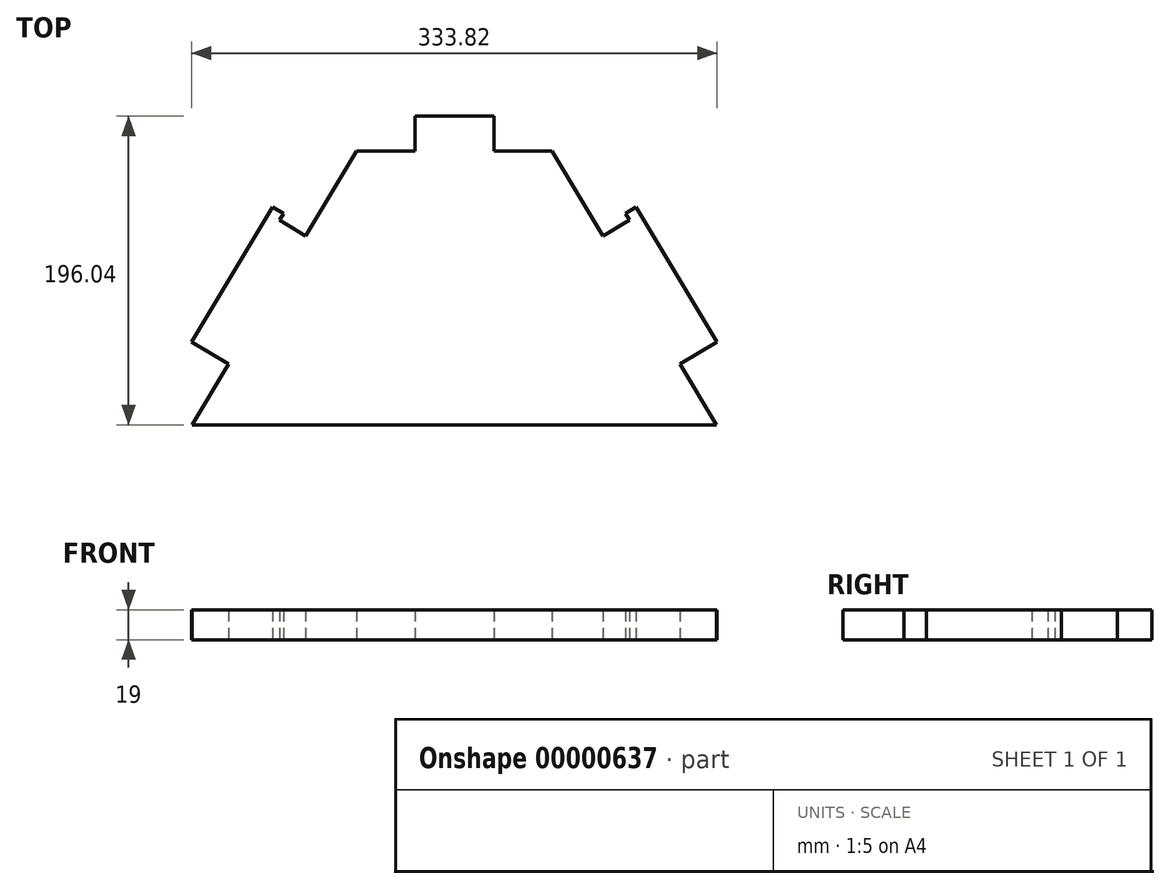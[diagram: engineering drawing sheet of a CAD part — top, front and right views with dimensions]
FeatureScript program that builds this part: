
annotation { "Feature Type Name" : "Feature", "Feature Type Description" : "" }
export const myFeature = defineFeature(function(context is Context, id is Id, definition is map)
    precondition{}
    {
        {
            var Q0;
            Q0=qCreatedBy(makeId("Top.planeOp"),FACE);
            var sketch = newSketch(context, id + "F0", { "sketchPlane" : qUnion([Q0])});
            skLineSegment(sketch, "E0", {"start": v(0, 22) * mm, "end": v(25, 22) * mm});
            skLineSegment(sketch, "E1", {"start": v(25, 22) * mm, "end": v(25, 0) * mm});
            skLineSegment(sketch, "E2", {"start": v(25, 0) * mm, "end": v(62, 0) * mm});
            skLineSegment(sketch, "E3", {"start": v(62, 0) * mm, "end": v(94.43, -54.01) * mm});
            skLineSegment(sketch, "E4", {"start": v(94.43, -54.01) * mm, "end": v(111.15, -43.97) * mm});
            skLineSegment(sketch, "E5", {"start": v(111.15, -43.97) * mm, "end": v(108.57, -39.69) * mm});
            skLineSegment(sketch, "E6", {"start": v(108.57, -39.69) * mm, "end": v(115.43, -35.57) * mm});
            skLineSegment(sketch, "E7", {"start": v(115.43, -35.57) * mm, "end": v(166.91, -121.3) * mm});
            skLineSegment(sketch, "E8", {"start": v(166.91, -121.3) * mm, "end": v(143.33, -135.46) * mm});
            skLineSegment(sketch, "E9", {"start": v(143.33, -135.46) * mm, "end": v(166.5, -174.04) * mm});
            skLineSegment(sketch, "E10", {"start": v(166.5, -174.04) * mm, "end": v(0, -174.04) * mm});
            skLineSegment(sketch, "E11", {"start": v(0, 22) * mm, "end": v(0, -174.04) * mm, "construction": true});
            skLineSegment(sketch, "E12.0.MirrorCS", {"start": v(-111.15, -43.97) * mm, "end": v(-108.57, -39.69) * mm});
            skLineSegment(sketch, "E12.1.MirrorCS", {"start": v(-62, 0) * mm, "end": v(-94.43, -54.01) * mm});
            skLineSegment(sketch, "E12.2.MirrorCS", {"start": v(0, 22) * mm, "end": v(-25, 22) * mm});
            skLineSegment(sketch, "E12.3.MirrorCS", {"start": v(-108.57, -39.69) * mm, "end": v(-115.43, -35.57) * mm});
            skLineSegment(sketch, "E12.4.MirrorCS", {"start": v(-166.91, -121.3) * mm, "end": v(-143.33, -135.46) * mm});
            skLineSegment(sketch, "E12.5.MirrorCS", {"start": v(-143.33, -135.46) * mm, "end": v(-166.5, -174.04) * mm});
            skLineSegment(sketch, "E12.6.MirrorCS", {"start": v(-166.5, -174.04) * mm, "end": v(0, -174.04) * mm});
            skLineSegment(sketch, "E12.7.MirrorCS", {"start": v(-94.43, -54.01) * mm, "end": v(-111.15, -43.97) * mm});
            skLineSegment(sketch, "E12.8.MirrorCS", {"start": v(-25, 0) * mm, "end": v(-62, 0) * mm});
            skLineSegment(sketch, "E12.9.MirrorCS", {"start": v(-115.43, -35.57) * mm, "end": v(-166.91, -121.3) * mm});
            skLineSegment(sketch, "E12.10.MirrorCS", {"start": v(-25, 22) * mm, "end": v(-25, 0) * mm});
            skSolve(sketch);
        }
        {
            var Q0;
            Q0=makeQuery(id+"F0.imprint","IMPRINT",FACE,{"disambiguationData":[TD([[makeQuery(id+"F0.imprint","IMPRINT",EDGE,{"derivedFrom":sQuery(id+"F0.wireOp",EDGE,"E0")}),-1.0]])]});
            extrude(context, id + "F1", {"entities" : qUnion([Q0]), "depth" : 19 * mm});
        }
    });
